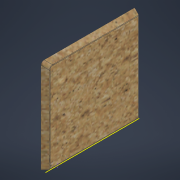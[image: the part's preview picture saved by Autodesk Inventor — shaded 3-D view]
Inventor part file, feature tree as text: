
AUTODESK INVENTOR PART (.ipt)
format: ipt  version: 2022 (Build 260153070, 153G)  size: 148,992 bytes
history: native  units: mm
features: other x5, sketch x3, chamfer x2, fillet x2, extrude x1
ambient origin geometry x8: Origin, YZ Plane, XZ Plane, XY Plane, X Axis, Y Axis, Z Axis, Center Point
bodies: Body1 (feature_tree)
feature tree (13):
  other  "Твердое тело1"
  other  "РабПлоскость1"
  extrude  "Выдавливание1"  Depth=16.0mm TaperAngle=0.0deg
  chamfer  "Фаска1"  Distance=16.0mm Angle=45.0deg
  sketch  "Эскиз2"
  sketch  "Эскиз3"
  chamfer  "Фаска2"  Distance=341.0mm
  fillet  "Сопряжение1"  Radius=341.0mm
  fillet  "Сопряжение2"  Radius=16.0mm
  sketch  "Эскиз1"
  other  "<userpath>\Documents\Inventor\TUTO\N_core.iam"
  other  "N_core.iam"
  other  "N_into_side:1"
